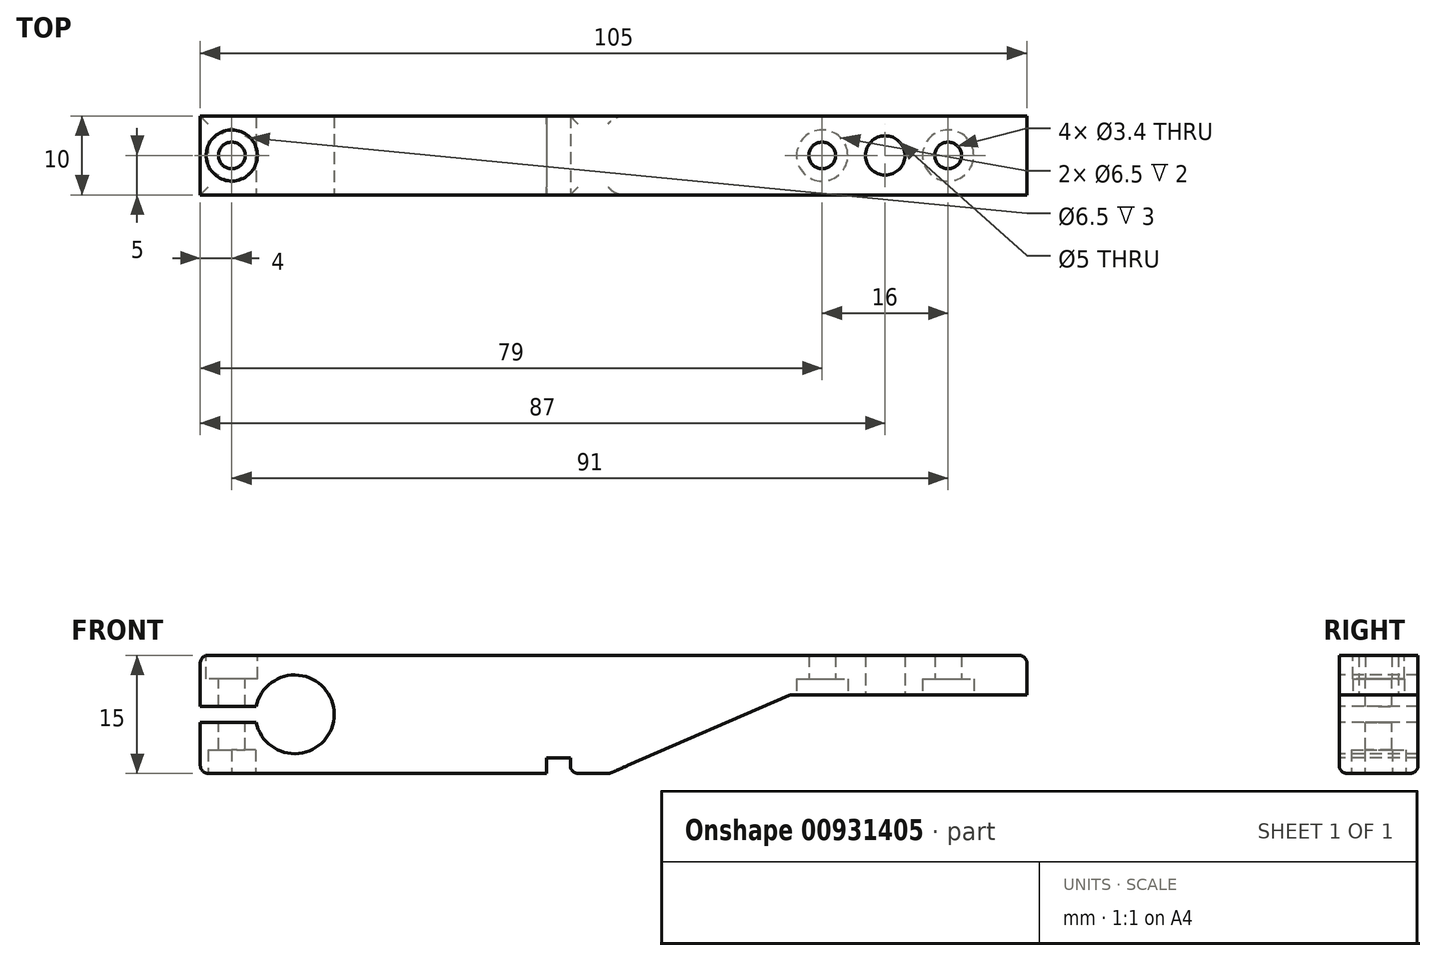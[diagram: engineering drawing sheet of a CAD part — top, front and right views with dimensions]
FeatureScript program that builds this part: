
annotation { "Feature Type Name" : "Feature", "Feature Type Description" : "" }
export const myFeature = defineFeature(function(context is Context, id is Id, definition is map)
    precondition{}
    {
        {
            var Q0;
            Q0=qCreatedBy(makeId("Top.planeOp"),FACE);
            var sketch = newSketch(context, id + "F0", { "sketchPlane" : qUnion([Q0])});
            skLineSegment(sketch, "E0.bottom", {"start": v(0, 0) * mm, "end": v(105, 0) * mm});
            skLineSegment(sketch, "E0.top", {"start": v(0, 10) * mm, "end": v(105, 10) * mm});
            skLineSegment(sketch, "E0.left", {"start": v(0, 0) * mm, "end": v(0, 10) * mm});
            skLineSegment(sketch, "E0.right", {"start": v(105, 0) * mm, "end": v(105, 10) * mm});
            skSolve(sketch);
        }
        {
            var Q0;
            Q0=makeQuery(id+"F0.imprint","IMPRINT",FACE,{"disambiguationData":[TD([[makeQuery(id+"F0.imprint","IMPRINT",EDGE,{"derivedFrom":sQuery(id+"F0.wireOp",EDGE,"E0.bottom")}),1.0]])]});
            extrude(context, id + "F1", {"entities" : qUnion([Q0]), "depth" : 15 * mm, "offsetDistance" : 25 * mm});
        }
        {
            var Q0;
            Q0=makeQuery(id+"F1.opExtrude","SWEPT_FACE",FACE,{"disambiguationData":[OSD([sQuery(id+"F0.wireOp",EDGE,"E0.bottom")])]});
            var sketch = newSketch(context, id + "F2", { "sketchPlane" : qUnion([Q0])});
            skArc(sketch, "E1", {"start": v(7.1, 6.5) * mm, "mid": v(17, 7.5) * mm, "end": v(7.1, 8.5) * mm});
            skLineSegment(sketch, "E2", {"start": v(105, 10) * mm, "end": v(75, 10) * mm});
            skLineSegment(sketch, "E3", {"start": v(75, 10) * mm, "end": v(52, 0) * mm});
            skLineSegment(sketch, "E4", {"start": v(52, 0) * mm, "end": v(105, 0) * mm});
            skLineSegment(sketch, "E5", {"start": v(105, 0) * mm, "end": v(105, 10) * mm});
            skLineSegment(sketch, "E6.bottom", {"start": v(0, 8.5) * mm, "end": v(7.1, 8.5) * mm});
            skLineSegment(sketch, "E6.top", {"start": v(0, 6.5) * mm, "end": v(7.1, 6.5) * mm});
            skLineSegment(sketch, "E6.left", {"start": v(0, 8.5) * mm, "end": v(0, 6.5) * mm});
            skLineSegment(sketch, "E7.bottom", {"start": v(44, 0) * mm, "end": v(47, 0) * mm});
            skLineSegment(sketch, "E7.top", {"start": v(44, 2) * mm, "end": v(47, 2) * mm});
            skLineSegment(sketch, "E7.left", {"start": v(44, 0) * mm, "end": v(44, 2) * mm});
            skLineSegment(sketch, "E7.right", {"start": v(47, 0) * mm, "end": v(47, 2) * mm});
            skSolve(sketch);
        }
        {
            var Q0;
            Q0=makeQuery(id+"F2.imprint","IMPRINT",FACE,{"disambiguationData":[TD([[makeQuery(id+"F2.imprint","IMPRINT",EDGE,{"derivedFrom":sQuery(id+"F2.wireOp",EDGE,"E2")}),1.0]])]});
            var Q1;
            Q1=makeQuery(id+"F2.imprint","IMPRINT",FACE,{"disambiguationData":[TD([[makeQuery(id+"F2.imprint","IMPRINT",EDGE,{"derivedFrom":sQuery(id+"F2.wireOp",EDGE,"E1")}),1.0]])]});
            var Q2;
            Q2=makeQuery(id+"F2.imprint","IMPRINT",FACE,{"disambiguationData":[TD([[makeQuery(id+"F2.imprint","IMPRINT",EDGE,{"derivedFrom":sQuery(id+"F2.wireOp",EDGE,"E7.bottom")}),1.0]])]});
            var Q3;
            Q3=makeQuery(id+"F2.imprint","IMPRINT",FACE,{"disambiguationData":[TD([[makeQuery(id+"F2.imprint","IMPRINT",EDGE,{"derivedFrom":sQuery(id+"F2.wireOp",EDGE,"mbcPeMDJ-fRm2-SM2C-fuVf-HlYfC1L1SrrV.bottom")}),-1.0]])]});
            extrude(context, id + "F3", {"entities" : qUnion([Q0, Q1, Q2, Q3]), "operationType" : NewBodyOperationType.REMOVE, "endBound" : BoundingType.UP_TO_NEXT, "oppositeDirection" : true, "depth" : 25 * mm, "offsetDistance" : 25 * mm});
        }
        {
            var Q0;
            Q0=makeQuery(id+"F1.opExtrude","CAP_FACE",FACE,{"disambiguationData":[OSD([sQuery(id+"F0.wireOp",EDGE,"E0.bottom"),sQuery(id+"F0.wireOp",EDGE,"E0.top"),sQuery(id+"F0.wireOp",EDGE,"E0.left"),sQuery(id+"F0.wireOp",EDGE,"E0.right")])],"isStart":true});
            var sketch = newSketch(context, id + "F4", { "sketchPlane" : qUnion([Q0])});
            skCircle(sketch, "E8.cCircle", {"center": v(4, -5) * mm, "radius": 3 * mm, "construction": true});
            skLineSegment(sketch, "E8.0", {"start": v(7, -6.73) * mm, "end": v(4, -8.46) * mm});
            skLineSegment(sketch, "E8.1", {"start": v(4, -8.46) * mm, "end": v(1, -6.73) * mm});
            skLineSegment(sketch, "E8.2", {"start": v(1, -6.73) * mm, "end": v(1, -3.27) * mm});
            skLineSegment(sketch, "E8.3", {"start": v(1, -3.27) * mm, "end": v(4, -1.54) * mm});
            skLineSegment(sketch, "E8.4", {"start": v(4, -1.54) * mm, "end": v(7, -3.27) * mm});
            skLineSegment(sketch, "E8.5", {"start": v(7, -3.27) * mm, "end": v(7, -6.73) * mm});
            skPoint(sketch, "E8.0.midPoint", {"position": v(5.5, -7.6) * mm});
            skSolve(sketch);
        }
        {
            var Q0;
            Q0=makeQuery(id+"F4.imprint","IMPRINT",FACE,{"disambiguationData":[TD([[makeQuery(id+"F4.imprint","IMPRINT",EDGE,{"derivedFrom":sQuery(id+"F4.wireOp",EDGE,"E8.0")}),-1.0]])]});
            extrude(context, id + "F5", {"entities" : qUnion([Q0]), "operationType" : NewBodyOperationType.REMOVE, "oppositeDirection" : true, "depth" : 3 * mm, "offsetDistance" : 25 * mm});
        }
        {
            var Q0;
            Q0=makeQuery(id+"F1.opExtrude","CAP_FACE",FACE,{"disambiguationData":[OSD([sQuery(id+"F0.wireOp",EDGE,"E0.bottom"),sQuery(id+"F0.wireOp",EDGE,"E0.top"),sQuery(id+"F0.wireOp",EDGE,"E0.left"),sQuery(id+"F0.wireOp",EDGE,"E0.right")])],"isStart":false});
            var sketch = newSketch(context, id + "F6", { "sketchPlane" : qUnion([Q0])});
            skPoint(sketch, "E9", {"position": v(4, 5) * mm});
            skSolve(sketch);
        }
        {
            var Q0;
            Q0=sQuery(id+"F6.wireOp",VERTEX,"E9");
            var Q1;
            Q1=makeQuery(id+"F1.opExtrude","SWEPT_BODY",BODY,{"disambiguationData":[OSD([sQuery(id+"F0.wireOp",EDGE,"E0.bottom"),sQuery(id+"F0.wireOp",EDGE,"E0.top"),sQuery(id+"F0.wireOp",EDGE,"E0.left"),sQuery(id+"F0.wireOp",EDGE,"E0.right")])]});
            hole(context, id + "F7", {"style" : HoleStyle.C_BORE, "endStyle" : HoleEndStyle.BLIND, "standardTappedOrClearance" : lookupTablePath({ "fit" : "Normal", "standard" : "ISO", "size" : "M3", "type" : "Clearance" }), "standardBlindInLast" : lookupTablePath({ "fit" : "Normal", "standard" : "ISO", "engagement" : "75%", "pitch" : "0.5 mm", "size" : "M3", "type" : "Clearance & tapped" }), "holeDiameter" : 3.4 * mm, "cBoreDiameter" : 6.5 * mm, "cBoreDepth" : 3 * mm, "majorDiameter" : 5 * mm, "holeDepth" : 15 * mm, "isTappedThrough" : true, "tappedDepth" : 12 * mm, "tapClearance" : 3, "locations" : qUnion([Q0]), "scope" : qUnion([Q1])});
        }
        {
            var Q0;
            Q0=makeQuery(id+"F3.boolean.opBoolean","COPY",FACE,{"derivedFrom":makeQuery(id+"F3.opExtrude","SWEPT_FACE",FACE,{"disambiguationData":[OSD([sQuery(id+"F2.wireOp",EDGE,"E2")])]})});
            var sketch = newSketch(context, id + "F8", { "sketchPlane" : qUnion([Q0])});
            skPoint(sketch, "E10", {"position": v(95, -5) * mm});
            skPoint(sketch, "E11", {"position": v(87, -5) * mm});
            skPoint(sketch, "E12", {"position": v(79, -5) * mm});
            skSolve(sketch);
        }
        {
            var Q0;
            Q0=sQuery(id+"F8.wireOp",VERTEX,"E11");
            var Q1;
            Q1=makeQuery(id+"F1.opExtrude","SWEPT_BODY",BODY,{"disambiguationData":[OSD([sQuery(id+"F0.wireOp",EDGE,"E0.bottom"),sQuery(id+"F0.wireOp",EDGE,"E0.top"),sQuery(id+"F0.wireOp",EDGE,"E0.left"),sQuery(id+"F0.wireOp",EDGE,"E0.right")])]});
            hole(context, id + "F9", {"style" : HoleStyle.SIMPLE, "endStyle" : HoleEndStyle.THROUGH, "holeDiameter" : 5 * mm, "majorDiameter" : 5 * mm, "isTappedThrough" : true, "tappedDepth" : 12 * mm, "tapClearance" : 3, "locations" : qUnion([Q0]), "scope" : qUnion([Q1])});
        }
        {
            var Q0;
            Q0=sQuery(id+"F8.wireOp",VERTEX,"E10");
            var Q1;
            Q1=sQuery(id+"F8.wireOp",VERTEX,"E12");
            var Q2;
            Q2=makeQuery(id+"F1.opExtrude","SWEPT_BODY",BODY,{"disambiguationData":[OSD([sQuery(id+"F0.wireOp",EDGE,"E0.bottom"),sQuery(id+"F0.wireOp",EDGE,"E0.top"),sQuery(id+"F0.wireOp",EDGE,"E0.left"),sQuery(id+"F0.wireOp",EDGE,"E0.right")])]});
            hole(context, id + "F10", {"style" : HoleStyle.C_BORE, "endStyle" : HoleEndStyle.THROUGH, "holeDiameter" : 3.4 * mm, "cBoreDiameter" : 6.5 * mm, "cBoreDepth" : 2 * mm, "majorDiameter" : 5 * mm, "isTappedThrough" : true, "tappedDepth" : 12 * mm, "tapClearance" : 3, "locations" : qUnion([Q0, Q1]), "scope" : qUnion([Q2])});
        }
        {
            var Q0;
            Q0=makeQuery(id+"F3.boolean.opBoolean","COPY",EDGE,{"derivedFrom":makeQuery(id+"F3.opExtrude","SWEPT_EDGE",EDGE,{"disambiguationData":[OSD([sQuery(id+"F2.wireOp",EDGE,"E2"),sQuery(id+"F2.wireOp",EDGE,"E3")])]})});
            var Q1;
            Q1=makeQuery(id+"F3.boolean.opBoolean","COPY",EDGE,{"derivedFrom":makeQuery(id+"F3.opExtrude","SWEPT_EDGE",EDGE,{"disambiguationData":[OSD([sQuery(id+"F0.wireOp",EDGE,"E0.bottom"),sQuery(id+"F2.wireOp",EDGE,"E3"),sQuery(id+"F2.wireOp",EDGE,"E4")])]})});
            var Q2;
            Q2=makeQuery(id+"F1.opExtrude","CAP_EDGE",EDGE,{"disambiguationData":[OSD([sQuery(id+"F0.wireOp",EDGE,"E0.left")])],"isStart":true});
            var Q3;
            Q3=makeQuery(id+"F1.opExtrude","CAP_EDGE",EDGE,{"disambiguationData":[OSD([sQuery(id+"F0.wireOp",EDGE,"E0.left")])],"isStart":false});
            var Q4;
            Q4=makeQuery(id+"F3.boolean.opBoolean","COPY",EDGE,{"derivedFrom":makeQuery(id+"F3.opExtrude","SWEPT_EDGE",EDGE,{"disambiguationData":[OSD([sQuery(id+"F0.wireOp",EDGE,"E0.bottom"),sQuery(id+"F0.wireOp",EDGE,"E0.right"),sQuery(id+"F2.wireOp",EDGE,"E2"),sQuery(id+"F2.wireOp",EDGE,"E5")])]})});
            var Q5;
            Q5=makeQuery(id+"F1.opExtrude","CAP_EDGE",EDGE,{"disambiguationData":[OSD([sQuery(id+"F0.wireOp",EDGE,"E0.right")])],"isStart":false});
            var Q6;
            Q6=makeQuery(id+"F3.boolean.opBoolean","COPY",EDGE,{"derivedFrom":makeQuery(id+"F3.opExtrude","SWEPT_EDGE",EDGE,{"disambiguationData":[OSD([sQuery(id+"F0.wireOp",EDGE,"E0.bottom"),sQuery(id+"F2.wireOp",EDGE,"mbcPeMDJ-fRm2-SM2C-fuVf-HlYfC1L1SrrV.bottom"),sQuery(id+"F2.wireOp",EDGE,"mbcPeMDJ-fRm2-SM2C-fuVf-HlYfC1L1SrrV.right")])]})});
            var Q7;
            Q7=makeQuery(id+"F3.boolean.opBoolean","COPY",EDGE,{"derivedFrom":makeQuery(id+"F3.opExtrude","SWEPT_EDGE",EDGE,{"disambiguationData":[OSD([sQuery(id+"F0.wireOp",EDGE,"E0.bottom"),sQuery(id+"F2.wireOp",EDGE,"mbcPeMDJ-fRm2-SM2C-fuVf-HlYfC1L1SrrV.bottom"),sQuery(id+"F2.wireOp",EDGE,"mbcPeMDJ-fRm2-SM2C-fuVf-HlYfC1L1SrrV.left")])]})});
            var Q8;
            Q8=makeQuery(id+"F3.boolean.opBoolean","COPY",EDGE,{"derivedFrom":makeQuery(id+"F3.opExtrude","SWEPT_EDGE",EDGE,{"disambiguationData":[OSD([sQuery(id+"F0.wireOp",EDGE,"E0.bottom"),sQuery(id+"F2.wireOp",EDGE,"E7.bottom"),sQuery(id+"F2.wireOp",EDGE,"E7.left")])]})});
            var Q9;
            Q9=makeQuery(id+"F3.boolean.opBoolean","COPY",EDGE,{"derivedFrom":makeQuery(id+"F3.opExtrude","SWEPT_EDGE",EDGE,{"disambiguationData":[OSD([sQuery(id+"F0.wireOp",EDGE,"E0.bottom"),sQuery(id+"F2.wireOp",EDGE,"E7.bottom"),sQuery(id+"F2.wireOp",EDGE,"E7.right")])]})});
            var Q10;
            {var subQ0=sQuery(id+"F0.wireOp",EDGE,"E0.left");var subQ1=sQuery(id+"F0.wireOp",EDGE,"E0.top");Q10=makeQuery(id+"F3.boolean.opBoolean","SPLIT",EDGE,{"disambiguationData":[TD([makeQuery(id+"F1.opExtrude","SWEPT_FACE",FACE,{"disambiguationData":[OSD([subQ0])]})])],"derivedFrom":makeQuery(id+"F1.opExtrude","CAP_EDGE",EDGE,{"disambiguationData":[OSD([subQ1])],"isStart":true})});}
            var Q11;
            {var subQ0=sQuery(id+"F0.wireOp",EDGE,"E0.top");Q11=makeQuery(id+"F3.boolean.opBoolean","SPLIT",EDGE,{"disambiguationData":[TD([makeQuery(id+"F3.opExtrude","SWEPT_FACE",FACE,{"disambiguationData":[OSD([sQuery(id+"F2.wireOp",EDGE,"E3")])]})])],"derivedFrom":makeQuery(id+"F1.opExtrude","CAP_EDGE",EDGE,{"disambiguationData":[OSD([subQ0])],"isStart":true})});}
            var Q12;
            Q12=makeQuery(id+"F3.boolean.opBoolean","COPY",EDGE,{"derivedFrom":makeQuery(id+"F3.opExtrude","CAP_EDGE",EDGE,{"disambiguationData":[OSD([sQuery(id+"F2.wireOp",EDGE,"E3")])],"isStart":false})});
            var Q13;
            Q13=makeQuery(id+"F3.boolean.opBoolean","COPY",EDGE,{"derivedFrom":makeQuery(id+"F3.opExtrude","CAP_EDGE",EDGE,{"disambiguationData":[OSD([sQuery(id+"F2.wireOp",EDGE,"E2")])],"isStart":false})});
            var Q14;
            Q14=makeQuery(id+"F3.boolean.opBoolean","COPY",EDGE,{"derivedFrom":makeQuery(id+"F3.opExtrude","CAP_EDGE",EDGE,{"disambiguationData":[OSD([sQuery(id+"F2.wireOp",EDGE,"E2")])],"isStart":true})});
            var Q15;
            Q15=makeQuery(id+"F3.boolean.opBoolean","COPY",EDGE,{"derivedFrom":makeQuery(id+"F3.opExtrude","CAP_EDGE",EDGE,{"disambiguationData":[OSD([sQuery(id+"F2.wireOp",EDGE,"E3")])],"isStart":true})});
            var Q16;
            {var subQ0=sQuery(id+"F0.wireOp",EDGE,"E0.bottom");Q16=makeQuery(id+"F3.boolean.opBoolean","SPLIT",EDGE,{"disambiguationData":[TD([makeQuery(id+"F3.opExtrude","SWEPT_FACE",FACE,{"disambiguationData":[OSD([sQuery(id+"F2.wireOp",EDGE,"E3")])]})])],"derivedFrom":makeQuery(id+"F1.opExtrude","CAP_EDGE",EDGE,{"disambiguationData":[OSD([subQ0])],"isStart":true})});}
            var Q17;
            {var subQ0=sQuery(id+"F0.wireOp",EDGE,"E0.bottom");var subQ1=sQuery(id+"F0.wireOp",EDGE,"E0.left");Q17=makeQuery(id+"F3.boolean.opBoolean","SPLIT",EDGE,{"disambiguationData":[TD([makeQuery(id+"F1.opExtrude","SWEPT_FACE",FACE,{"disambiguationData":[OSD([subQ1])]})])],"derivedFrom":makeQuery(id+"F1.opExtrude","CAP_EDGE",EDGE,{"disambiguationData":[OSD([subQ0])],"isStart":true})});}
            fillet(context, id + "F11", {"entities" : qUnion([Q0, Q1, Q2, Q3, Q4, Q5, Q6, Q7, Q8, Q9, Q10, Q11, Q12, Q13, Q14, Q15, Q16, Q17]), "tangentPropagation" : true, "radius" : 1 * mm, "defaultsChanged" : false, "vertexSettings" : [], "allowEdgeOverflow" : false});
        }
    });
